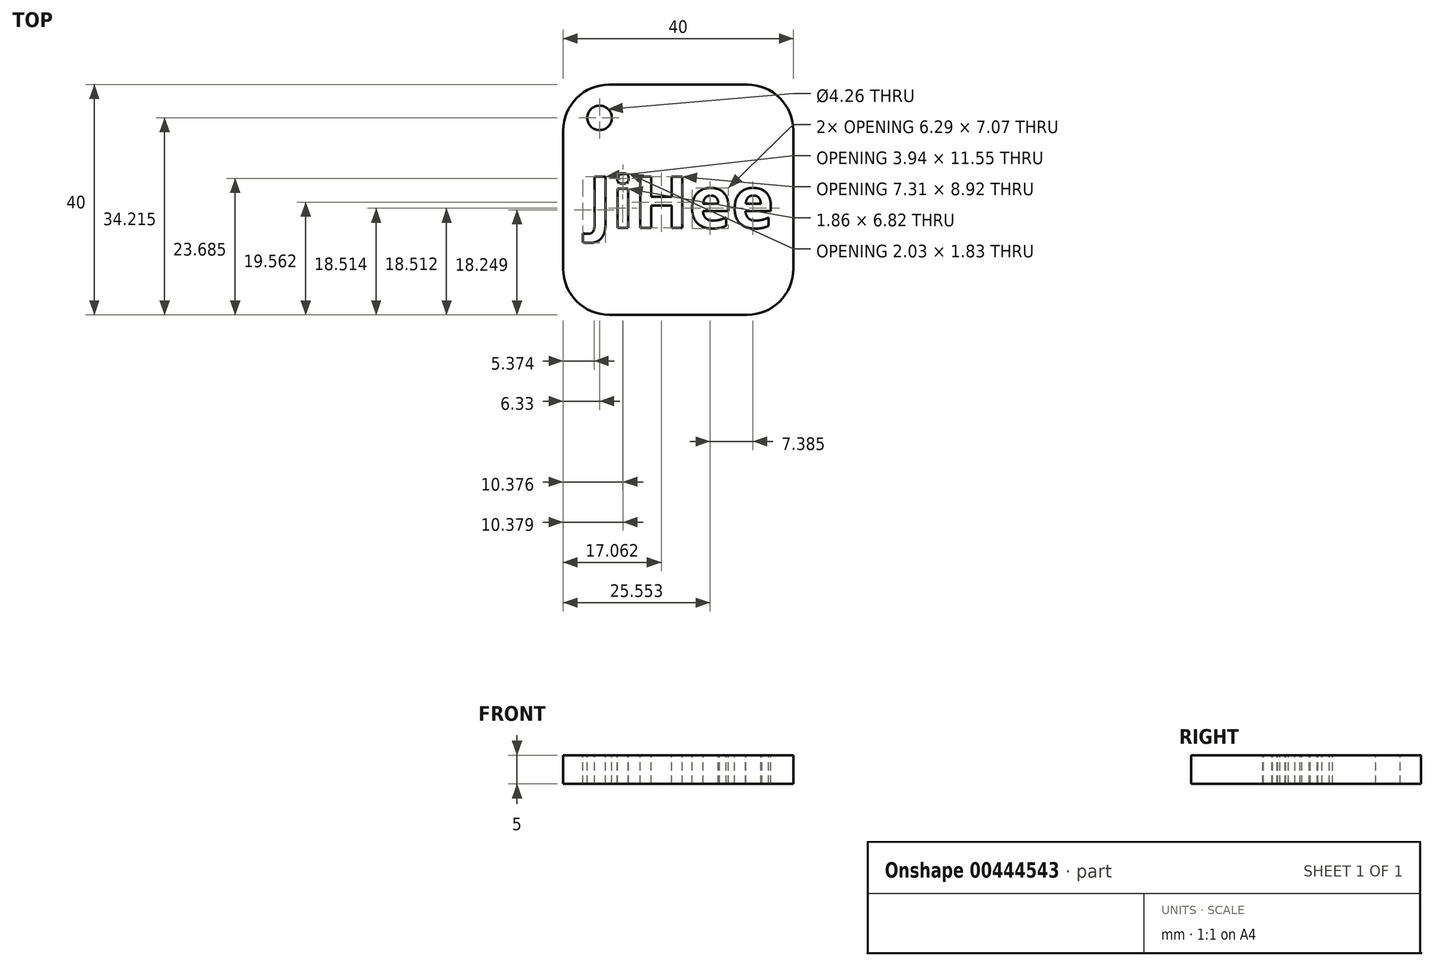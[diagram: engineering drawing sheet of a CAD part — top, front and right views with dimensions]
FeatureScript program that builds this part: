
annotation { "Feature Type Name" : "Feature", "Feature Type Description" : "" }
export const myFeature = defineFeature(function(context is Context, id is Id, definition is map)
    precondition{}
    {
        {
            var Q0;
            Q0=qCreatedBy(makeId("Top.planeOp"),FACE);
            var sketch = newSketch(context, id + "F0", { "sketchPlane" : qUnion([Q0])});
            skLineSegment(sketch, "E0.bottom", {"start": v(12, 20) * mm, "end": v(-12, 20) * mm});
            skLineSegment(sketch, "E0.top", {"start": v(12, -20) * mm, "end": v(-12, -20) * mm});
            skLineSegment(sketch, "E0.left", {"start": v(20, 12) * mm, "end": v(20, -12) * mm});
            skLineSegment(sketch, "E0.right", {"start": v(-20, 12) * mm, "end": v(-20, -12) * mm});
            skPoint(sketch, "E0.middle", {"position": v(0, 0) * mm});
            skPoint(sketch, "E1.visualSharp", {"position": v(-20, 20) * mm});
            skArc(sketch, "E1.filletArc", {"start": v(-12, 20) * mm, "mid": v(-17.66, 17.66) * mm, "end": v(-20, 12) * mm});
            skPoint(sketch, "E2.visualSharp", {"position": v(-20, -20) * mm});
            skArc(sketch, "E2.filletArc", {"start": v(-20, -12) * mm, "mid": v(-17.66, -17.66) * mm, "end": v(-12, -20) * mm});
            skPoint(sketch, "E3.visualSharp", {"position": v(20, 20) * mm});
            skArc(sketch, "E3.filletArc", {"start": v(20, 12) * mm, "mid": v(17.66, 17.66) * mm, "end": v(12, 20) * mm});
            skPoint(sketch, "E4.visualSharp", {"position": v(20, -20) * mm});
            skArc(sketch, "E4.filletArc", {"start": v(12, -20) * mm, "mid": v(17.66, -17.66) * mm, "end": v(20, -12) * mm});
            skSolve(sketch);
        }
        {
            var Q0;
            Q0 = qSketchRegion(id + "F0", true);
            extrude(context, id + "F1", {"entities" : qUnion([Q0]), "depth" : 5 * mm});
        }
        {
            var Q0;
            Q0=makeQuery(id+"F1.opExtrude","CAP_FACE",FACE,{"disambiguationData":[OSD([sQuery(id+"F0.wireOp",EDGE,"E0.bottom"),sQuery(id+"F0.wireOp",EDGE,"E0.top"),sQuery(id+"F0.wireOp",EDGE,"E0.left"),sQuery(id+"F0.wireOp",EDGE,"E0.right"),sQuery(id+"F0.wireOp",EDGE,"E1.filletArc"),sQuery(id+"F0.wireOp",EDGE,"E2.filletArc"),sQuery(id+"F0.wireOp",EDGE,"E3.filletArc"),sQuery(id+"F0.wireOp",EDGE,"E4.filletArc")])],"isStart":false});
            var sketch = newSketch(context, id + "F2", { "sketchPlane" : qUnion([Q0])});
            skText(sketch, "E5", { "text": "JiHee", "fontName": "OpenSans-Bold.ttf"});
            skCircle(sketch, "E6", {"center": v(-13.67, 14.22) * mm, "radius": 2.13 * mm});
            const initialGuessF2  = {"E5": [-0.01567, -0.0049, 1, 0, 0.009]};
            skSetInitialGuess(sketch, initialGuessF2);
            skSolve(sketch);
        }
        {
            var Q0;
            Q0 = qSketchRegion(id + "F2", true);
            extrude(context, id + "F3", {"entities" : qUnion([Q0]), "operationType" : NewBodyOperationType.REMOVE, "oppositeDirection" : true, "depth" : 10 * mm});
        }
    });
